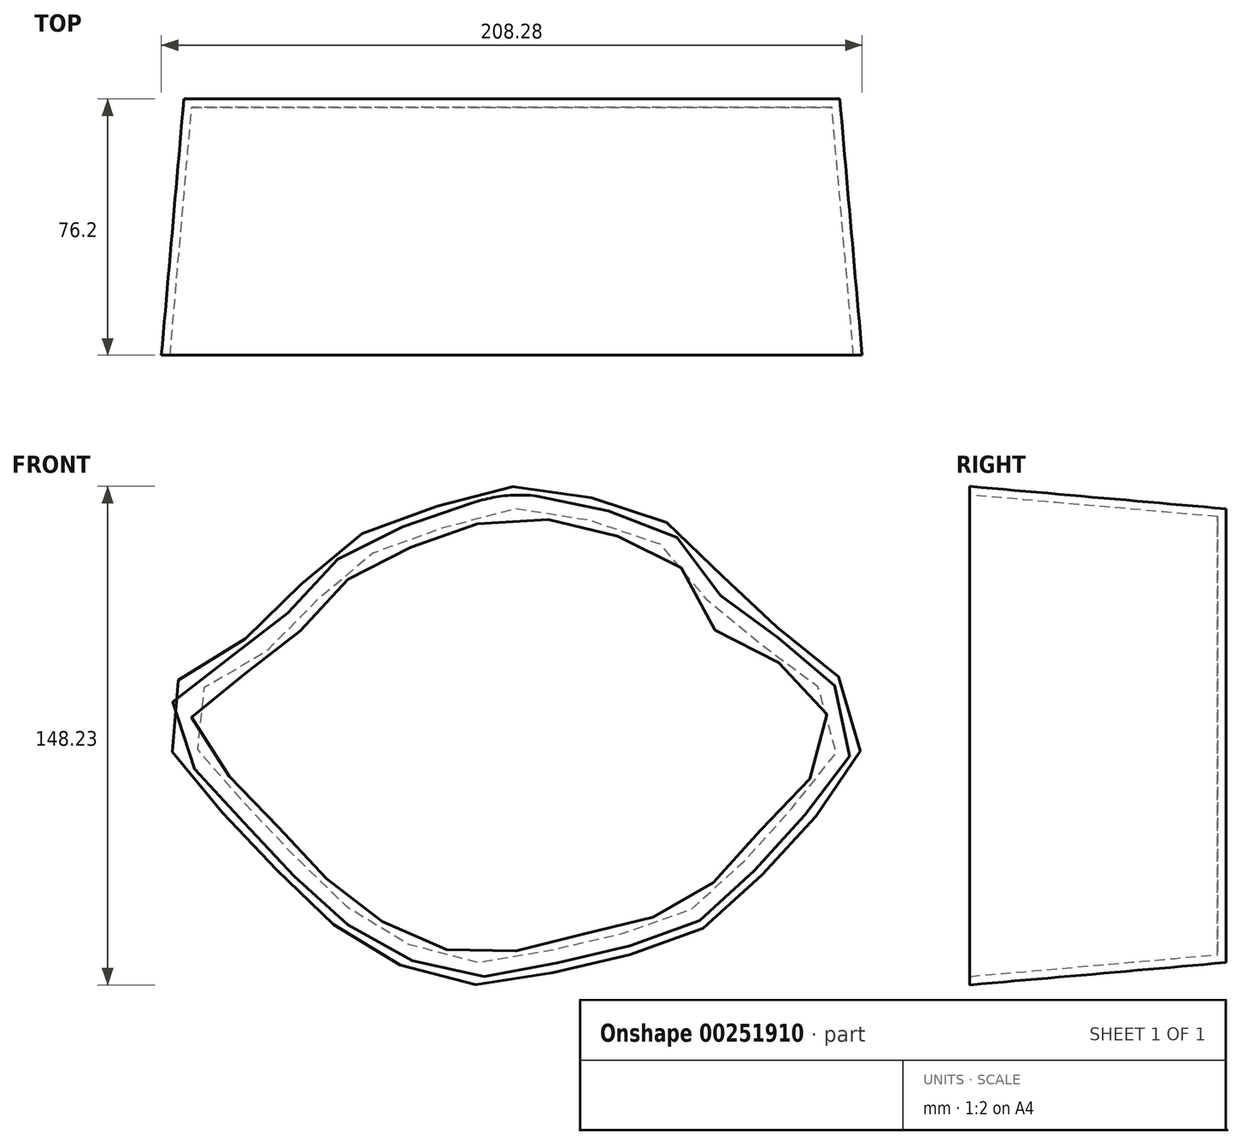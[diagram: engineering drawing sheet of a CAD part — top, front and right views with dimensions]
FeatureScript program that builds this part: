
annotation { "Feature Type Name" : "Feature", "Feature Type Description" : "" }
export const myFeature = defineFeature(function(context is Context, id is Id, definition is map)
    precondition{}
    {
        {
            var Q0;
            Q0=qCreatedBy(makeId("Front.planeOp"),FACE);
            var sketch = newSketch(context, id + "F0", { "sketchPlane" : qUnion([Q0])});
            skPoint(sketch, "E0.visualSharp", {"position": v(-68.67, 60.85) * mm});
            skPoint(sketch, "E1.visualSharp", {"position": v(-68.67, -40.75) * mm});
            skPoint(sketch, "E2.visualSharp", {"position": v(83.73, -40.75) * mm});
            skPoint(sketch, "E3.visualSharp", {"position": v(83.73, 60.85) * mm});
            skFitSpline(sketch, "E4", {"points": [v(-43.27, 60.85) * mm, v(-68.67, 35.45) * mm, v(-92.5, 17.65) * mm, v(-68.67, -15.35) * mm, v(-43.27, -40.75) * mm, v(-7.55, -56.48) * mm, v(22.8, -51.3) * mm, v(58.33, -40.75) * mm, v(83.73, -15.35) * mm, v(102.35, 10.82) * mm, v(83.73, 35.45) * mm, v(66.1, 44.71) * mm, v(58.33, 60.85) * mm, v(28.7, 74.6) * mm, v(2.67, 77.98) * mm, v(-19.16, 71.26) * mm, v(-43.27, 60.85) * mm]});
            skSolve(sketch);
        }
        {
            var Q0;
            Q0 = qSketchRegion(id + "F0", true);
            extrude(context, id + "F1", {"entities" : qUnion([Q0]), "depth" : 76.2 * mm, "hasDraft" : true, "draftAngle" : 5 * degree});
        }
        {
            var Q0;
            Q0=makeQuery(id+"F1.opExtrude","CAP_FACE",FACE,{"disambiguationData":[OSD([sQuery(id+"F0.wireOp",EDGE,"E4")])],"isStart":false});
            shell(context, id + "F2", {"entities" : qUnion([Q0]), "thickness" : 2.54 * mm});
        }
    });
